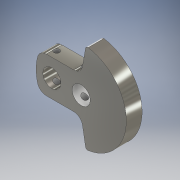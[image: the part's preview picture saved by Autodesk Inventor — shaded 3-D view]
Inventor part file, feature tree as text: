
AUTODESK INVENTOR PART (.ipt)
format: ipt  version: 2017 (Build 210142000, 142)  size: 219,136 bytes
history: native  units: mm
features: extrude x4, fillet x4, sketch x2, plane x2, projected_geometry x2
ambient origin geometry x8: Origin, YZ Plane, XZ Plane, XY Plane, X Axis, Y Axis, Z Axis, Center Point
bodies: Body1 (feature_tree)
feature tree (14):
  sketch  "Sketch1"  dims[d0=40.0mm d1=8.0mm]
  extrude  "Extrusion4"  Depth=8.0mm
  extrude  "Extrusion5"  Depth=10.0mm
  fillet  "Fillet1"  Radius=20.0mm
  fillet  "Fillet2"  Radius=17.453293mm
  fillet  "Fillet3"  Radius=17.453293mm
  fillet  "Fillet4"  Radius=40.0mm
  plane  "Work Plane1"
  extrude  "Extrusion6"  Depth=10.0mm
  plane  "Work Plane2"
  extrude  "Extrusion7"  Depth=10.0mm
  sketch  "Sketch3"  dims[d2=16.0mm d3=20.0mm d4=20.0mm d5=17.453293mm d6=17.453293mm d7=40.0mm d8=20.0mm d10=8.0mm d14=8.0mm d15=13.0mm d16=13.0mm d21=7.0mm d24=7.0mm d25=0.0mm d26=7.8mm d27=0.0mm d28=4.0mm d29=4.0mm d30=4.0mm d31=1.0mm d32=0.0mm d33=2.5mm d34=11.0mm d35=3.497732mm d37=10.0mm d38=0.0mm d39=11.5mm d43=10.0mm d44=0.0mm d45=5.0mm d46=7.0mm d47=5.0mm d48=3.5mm d50=2.5mm]
  projected_geometry  "Projected Loop1"
  projected_geometry  "Projected Loop2"
